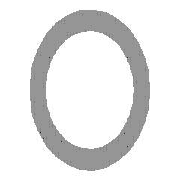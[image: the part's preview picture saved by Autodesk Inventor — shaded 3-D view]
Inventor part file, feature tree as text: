
AUTODESK INVENTOR PART (.ipt)
format: ipt  version: 2013 (Build 170138000, 138)  size: 126,464 bytes
history: native  units: mm (DEFAULTED — no unit token found)
features: other x4, plane x4, sketch x4, extrude x1
ambient origin geometry x8: Origin, YZ Plane, XZ Plane, XY Plane, X Axis, Y Axis, Z Axis, Center Point
bodies: Solid1 (feature_tree), Body (feature_tree)
feature tree (13):
  parser-record x1  (decoder bookkeeping rows leaked as tree rows — omitted from the tree; the rows remain in map.json)
  other  "Driven Length"
  other  "Start plane"
  other  "End plane"
  plane  "Work Plane4"
  plane  "Work Plane5"
  plane  "Work Plane6"
  extrude  "Extrusion2"  Depth=3.3782mm
  sketch  "Sketch"  dims[d5=111.252mm d6=90.0deg d7=111.252mm d8=3.302mm d9=0.0mm]
  sketch  "Sketch3"  dims[d0=33.401mm d1=3.3782mm]
  plane  "Work Plane3"
  sketch  "Sketch4"  dims[d2=111.252mm d3=0.0mm]
  sketch  "Sketch5"  dims[d4=-0.0mm]
